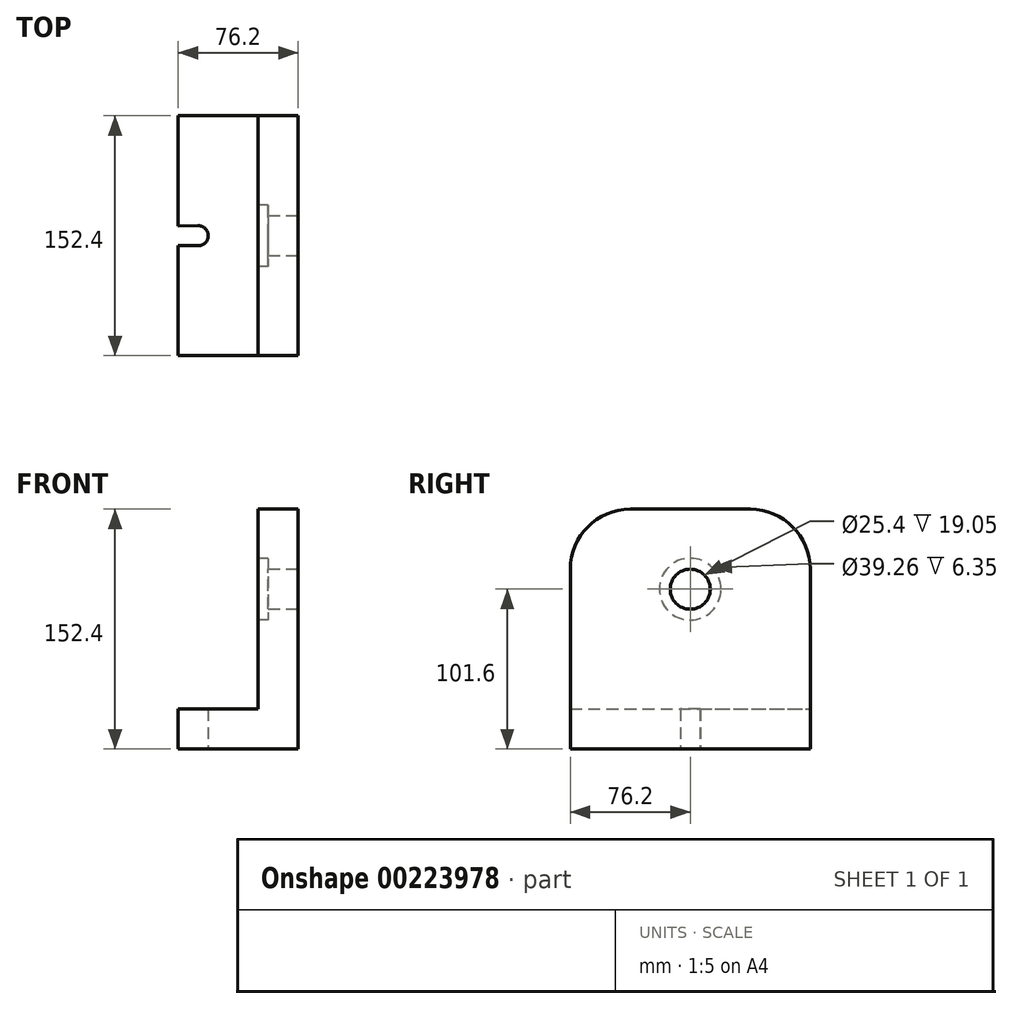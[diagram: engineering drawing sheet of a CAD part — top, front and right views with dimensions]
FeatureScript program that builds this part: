
annotation { "Feature Type Name" : "Feature", "Feature Type Description" : "" }
export const myFeature = defineFeature(function(context is Context, id is Id, definition is map)
    precondition{}
    {
        {
            var Q0;
            Q0=qCreatedBy(makeId("Front.planeOp"),FACE);
            var sketch = newSketch(context, id + "F0", { "sketchPlane" : qUnion([Q0])});
            skLineSegment(sketch, "E0", {"start": v(0, 0) * mm, "end": v(-76.2, 0) * mm});
            skLineSegment(sketch, "E1", {"start": v(-76.2, 0) * mm, "end": v(-76.2, 25.4) * mm});
            skLineSegment(sketch, "E2", {"start": v(-76.2, 25.4) * mm, "end": v(-25.4, 25.4) * mm});
            skLineSegment(sketch, "E3", {"start": v(-25.4, 25.4) * mm, "end": v(-25.4, 152.4) * mm});
            skLineSegment(sketch, "E4", {"start": v(-25.4, 152.4) * mm, "end": v(0, 152.4) * mm});
            skLineSegment(sketch, "E5", {"start": v(0, 152.4) * mm, "end": v(0, 0) * mm});
            skSolve(sketch);
        }
        {
            var Q0;
            Q0=makeQuery(id+"F0.imprint","IMPRINT",FACE,{"disambiguationData":[TD([[makeQuery(id+"F0.imprint","IMPRINT",EDGE,{"derivedFrom":sQuery(id+"F0.wireOp",EDGE,"E0")}),-1.0]])]});
            extrude(context, id + "F1", {"entities" : qUnion([Q0]), "endBound" : BoundingType.SYMMETRIC, "depth" : 152.4 * mm});
        }
        {
            var Q0;
            Q0=makeQuery(id+"F1.opExtrude","SWEPT_FACE",FACE,{"disambiguationData":[OSD([sQuery(id+"F0.wireOp",EDGE,"E5")])]});
            var sketch = newSketch(context, id + "F2", { "sketchPlane" : qUnion([Q0])});
            skCircle(sketch, "E6", {"center": v(0, 101.6) * mm, "radius": 12.7 * mm});
            skSolve(sketch);
        }
        {
            var Q0;
            Q0=makeQuery(id+"F2.imprint","IMPRINT",FACE,{"disambiguationData":[TD([[makeQuery(id+"F2.imprint","IMPRINT",EDGE,{"derivedFrom":sQuery(id+"F2.wireOp",EDGE,"E6")}),1.0]])]});
            extrude(context, id + "F3", {"entities" : qUnion([Q0]), "operationType" : NewBodyOperationType.REMOVE, "oppositeDirection" : true, "depth" : 25.4 * mm});
        }
        {
            var Q0;
            Q0=makeQuery(id+"F1.opExtrude","SWEPT_FACE",FACE,{"disambiguationData":[OSD([sQuery(id+"F0.wireOp",EDGE,"E0")])]});
            var sketch = newSketch(context, id + "F4", { "sketchPlane" : qUnion([Q0])});
            skCircle(sketch, "E7", {"center": v(-63.43, 0) * mm, "radius": 6.35 * mm});
            skLineSegment(sketch, "E8", {"start": v(-63.5, 6.35) * mm, "end": v(-76.2, 6.21) * mm});
            skLineSegment(sketch, "E9", {"start": v(-63.5, -6.35) * mm, "end": v(-76.2, -6.21) * mm});
            skSolve(sketch);
        }
        {
            var Q0;
            {var subQ0=sQuery(id+"F4.wireOp",EDGE,"E8");Q0=makeQuery(id+"F4.imprint","IMPRINT",FACE,{"disambiguationData":[TD([[makeQuery(id+"F4.imprint","IMPRINT",EDGE,{"derivedFrom":subQ0}),1.0]])]});}
            var Q1;
            {var subQ0=sQuery(id+"F4.wireOp",EDGE,"E7");var subQ1=makeQuery(id+"F4.imprint","INTERSECT",VERTEX,{"derivedFrom":[subQ0,sQuery(id+"F4.wireOp",EDGE,"E8")]});Q1=makeQuery(id+"F4.imprint","IMPRINT",FACE,{"disambiguationData":[TD([[makeQuery(id+"F4.imprint","IMPRINT",EDGE,{"disambiguationData":[TD([[subQ1,-1.0]])],"derivedFrom":subQ0}),1.0]])]});}
            extrude(context, id + "F5", {"entities" : qUnion([Q0, Q1]), "operationType" : NewBodyOperationType.REMOVE, "oppositeDirection" : true, "depth" : 25.4 * mm});
        }
        {
            var Q0;
            Q0=makeQuery(id+"F1.opExtrude","CAP_EDGE",EDGE,{"disambiguationData":[OSD([sQuery(id+"F0.wireOp",EDGE,"E4")])],"isStart":false});
            fillet(context, id + "F6", {"entities" : qUnion([Q0]), "radius" : 38.1 * mm, "tangentPropagation" : true, "allowEdgeOverflow" : false});
        }
        {
            var Q0;
            Q0=makeQuery(id+"F1.opExtrude","CAP_EDGE",EDGE,{"disambiguationData":[OSD([sQuery(id+"F0.wireOp",EDGE,"E4")])],"isStart":true});
            fillet(context, id + "F7", {"entities" : qUnion([Q0]), "radius" : 38.1 * mm, "tangentPropagation" : true, "allowEdgeOverflow" : false});
        }
        {
            var Q0;
            Q0=makeQuery(id+"F1.opExtrude","SWEPT_FACE",FACE,{"disambiguationData":[OSD([sQuery(id+"F0.wireOp",EDGE,"E3")])]});
            var sketch = newSketch(context, id + "F8", { "sketchPlane" : qUnion([Q0])});
            skCircle(sketch, "E10", {"center": v(0, 101.6) * mm, "radius": 19.63 * mm});
            skSolve(sketch);
        }
        {
            var Q0;
            Q0=makeQuery(id+"F8.imprint","IMPRINT",FACE,{"disambiguationData":[TD([[makeQuery(id+"F8.imprint","IMPRINT",EDGE,{"derivedFrom":sQuery(id+"F8.wireOp",EDGE,"E10")}),1.0]])]});
            extrude(context, id + "F9", {"entities" : qUnion([Q0]), "operationType" : NewBodyOperationType.REMOVE, "oppositeDirection" : true, "depth" : 6.35 * mm});
        }
    });
